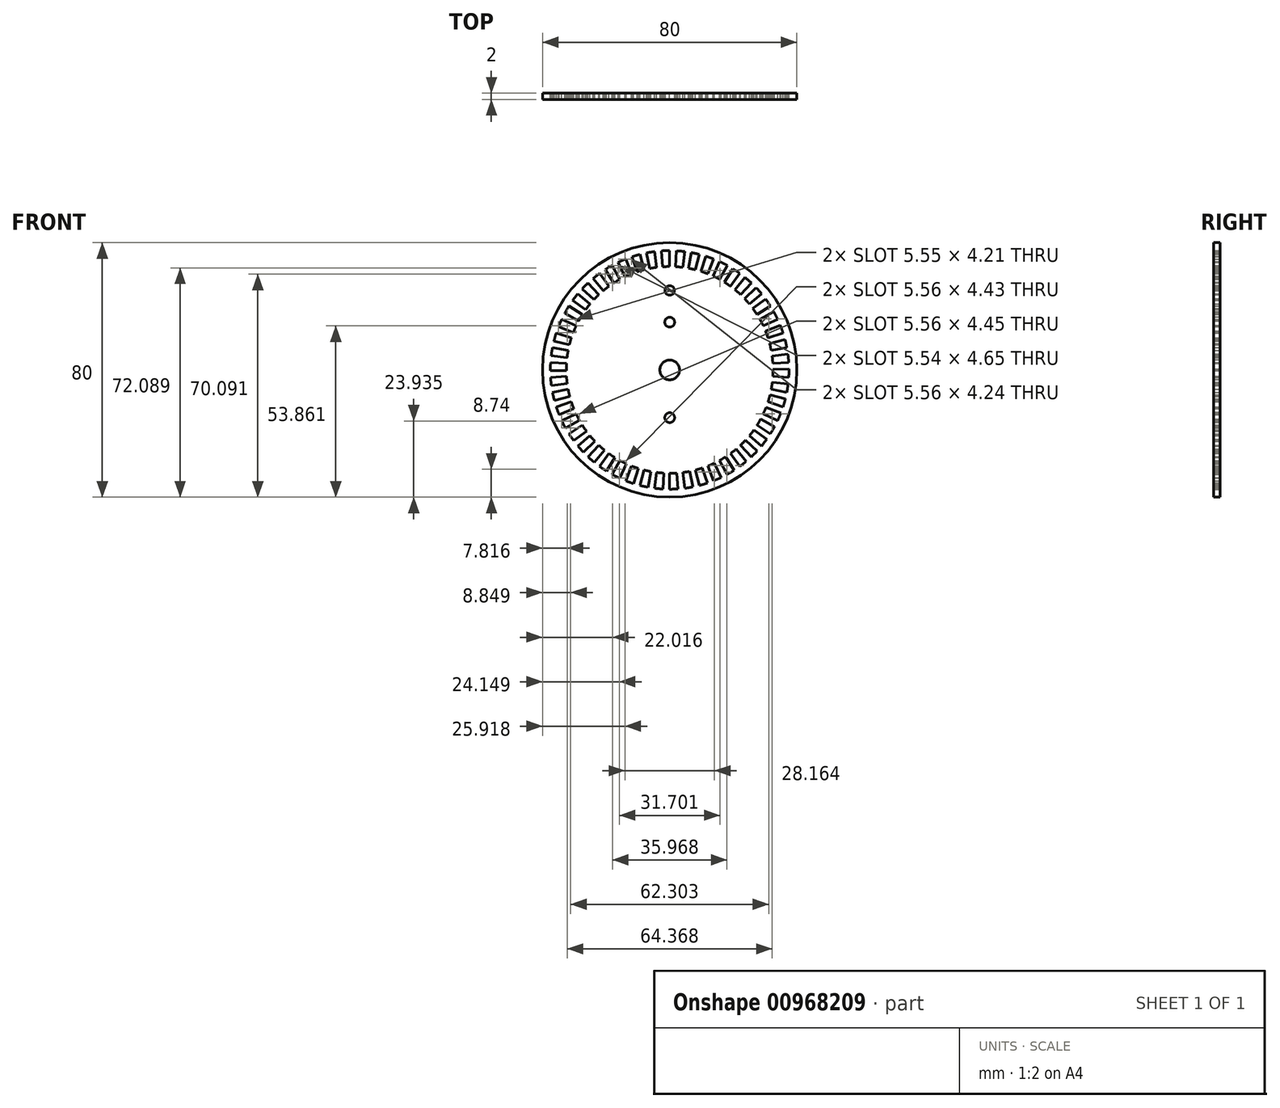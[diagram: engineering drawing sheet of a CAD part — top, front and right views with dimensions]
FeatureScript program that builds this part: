
annotation { "Feature Type Name" : "Feature", "Feature Type Description" : "" }
export const myFeature = defineFeature(function(context is Context, id is Id, definition is map)
    precondition{}
    {
        {
            var Q0;
            Q0=qCreatedBy(makeId("Front.planeOp"),FACE);
            var sketch = newSketch(context, id + "F0", { "sketchPlane" : qUnion([Q0])});
            skCircle(sketch, "E0", {"center": v(0, 0) * mm, "radius": 40 * mm});
            skSolve(sketch);
        }
        {
            var Q0;
            Q0 = qSketchRegion(id + "F0", true);
            extrude(context, id + "F1", {"entities" : qUnion([Q0]), "endBound" : BoundingType.SYMMETRIC, "depth" : 2 * mm, "offsetDistance" : 25 * mm});
        }
        {
            var Q0;
            Q0=qCreatedBy(makeId("Front.planeOp"),FACE);
            var sketch = newSketch(context, id + "F2", { "sketchPlane" : qUnion([Q0])});
            skCircle(sketch, "E1", {"center": v(0, 0) * mm, "radius": 3.1 * mm});
            skCircle(sketch, "E2", {"center": v(0, 25) * mm, "radius": 1.5 * mm});
            skCircle(sketch, "E3", {"center": v(0, 15) * mm, "radius": 1.55 * mm});
            skCircle(sketch, "E4", {"center": v(0, -15) * mm, "radius": 1.55 * mm});
            skSolve(sketch);
        }
        {
            var Q0;
            Q0 = qSketchRegion(id + "F2", true);
            extrude(context, id + "F3", {"entities" : qUnion([Q0]), "operationType" : NewBodyOperationType.REMOVE, "endBound" : BoundingType.SYMMETRIC, "oppositeDirection" : true, "depth" : 12 * mm, "offsetDistance" : 25 * mm});
        }
        {
            var Q0;
            Q0=qCreatedBy(makeId("Front.planeOp"),FACE);
            var sketch = newSketch(context, id + "F4", { "sketchPlane" : qUnion([Q0])});
            skLineSegment(sketch, "E5", {"start": v(0, 32.5) * mm, "end": v(0, 37.5) * mm});
            skArc(sketch, "E6", {"start": v(0, 37.5) * mm, "mid": v(-1.3, 37.48) * mm, "end": v(-2.61, 37.4) * mm});
            skArc(sketch, "E7", {"start": v(0, 32.5) * mm, "mid": v(-1.13, 32.48) * mm, "end": v(-2.26, 32.42) * mm});
            skLineSegment(sketch, "E8", {"start": v(-2.26, 32.42) * mm, "end": v(-2.61, 37.4) * mm});
            skLineSegment(sketch, "E9.1.0", {"start": v(-6.3, 31.88) * mm, "end": v(-7.28, 36.79) * mm});
            skLineSegment(sketch, "E9.1.1", {"start": v(-4.07, 32.24) * mm, "end": v(-4.7, 37.2) * mm});
            skArc(sketch, "E9.1.2", {"start": v(-4.7, 37.2) * mm, "mid": v(-6, 37.02) * mm, "end": v(-7.28, 36.79) * mm});
            skArc(sketch, "E9.1.3", {"start": v(-4.07, 32.24) * mm, "mid": v(-5.2, 32.08) * mm, "end": v(-6.3, 31.88) * mm});
            skLineSegment(sketch, "E9.2.0", {"start": v(-10.26, 30.84) * mm, "end": v(-11.83, 35.58) * mm});
            skLineSegment(sketch, "E9.2.1", {"start": v(-8.08, 31.48) * mm, "end": v(-9.33, 36.32) * mm});
            skArc(sketch, "E9.2.2", {"start": v(-9.33, 36.32) * mm, "mid": v(-10.59, 35.97) * mm, "end": v(-11.83, 35.58) * mm});
            skArc(sketch, "E9.2.3", {"start": v(-8.08, 31.48) * mm, "mid": v(-9.17, 31.18) * mm, "end": v(-10.26, 30.84) * mm});
            skLineSegment(sketch, "E9.3.0", {"start": v(-14.04, 29.31) * mm, "end": v(-16.2, 33.82) * mm});
            skLineSegment(sketch, "E9.3.1", {"start": v(-11.96, 30.22) * mm, "end": v(-13.8, 34.87) * mm});
            skArc(sketch, "E9.3.2", {"start": v(-13.8, 34.87) * mm, "mid": v(-15.01, 34.36) * mm, "end": v(-16.2, 33.82) * mm});
            skArc(sketch, "E9.3.3", {"start": v(-11.96, 30.22) * mm, "mid": v(-13, 29.78) * mm, "end": v(-14.04, 29.31) * mm});
            skLineSegment(sketch, "E9.4.0", {"start": v(-17.6, 27.32) * mm, "end": v(-20.31, 31.52) * mm});
            skLineSegment(sketch, "E9.4.1", {"start": v(-15.66, 28.48) * mm, "end": v(-18.07, 32.86) * mm});
            skArc(sketch, "E9.4.2", {"start": v(-18.07, 32.86) * mm, "mid": v(-19.2, 32.21) * mm, "end": v(-20.31, 31.52) * mm});
            skArc(sketch, "E9.4.3", {"start": v(-15.66, 28.48) * mm, "mid": v(-16.64, 27.92) * mm, "end": v(-17.6, 27.32) * mm});
            skLineSegment(sketch, "E9.5.0", {"start": v(-20.89, 24.9) * mm, "end": v(-24.1, 28.73) * mm});
            skLineSegment(sketch, "E9.5.1", {"start": v(-19.1, 26.3) * mm, "end": v(-22.04, 30.34) * mm});
            skArc(sketch, "E9.5.2", {"start": v(-22.04, 30.34) * mm, "mid": v(-23.09, 29.55) * mm, "end": v(-24.1, 28.73) * mm});
            skArc(sketch, "E9.5.3", {"start": v(-19.1, 26.3) * mm, "mid": v(-20, 25.61) * mm, "end": v(-20.89, 24.9) * mm});
            skLineSegment(sketch, "E9.6.0", {"start": v(-23.84, 22.08) * mm, "end": v(-27.51, 25.48) * mm});
            skLineSegment(sketch, "E9.6.1", {"start": v(-22.25, 23.7) * mm, "end": v(-25.67, 27.34) * mm});
            skArc(sketch, "E9.6.2", {"start": v(-25.67, 27.34) * mm, "mid": v(-26.6, 26.43) * mm, "end": v(-27.51, 25.48) * mm});
            skArc(sketch, "E9.6.3", {"start": v(-22.25, 23.7) * mm, "mid": v(-23.06, 22.9) * mm, "end": v(-23.84, 22.08) * mm});
            skLineSegment(sketch, "E9.7.0", {"start": v(-26.42, 18.92) * mm, "end": v(-30.49, 21.83) * mm});
            skLineSegment(sketch, "E9.7.1", {"start": v(-25.04, 20.72) * mm, "end": v(-28.9, 23.9) * mm});
            skArc(sketch, "E9.7.2", {"start": v(-28.9, 23.9) * mm, "mid": v(-29.7, 22.88) * mm, "end": v(-30.49, 21.83) * mm});
            skArc(sketch, "E9.7.3", {"start": v(-25.04, 20.72) * mm, "mid": v(-25.75, 19.83) * mm, "end": v(-26.42, 18.92) * mm});
            skLineSegment(sketch, "E9.8.0", {"start": v(-28.59, 15.46) * mm, "end": v(-32.98, 17.84) * mm});
            skLineSegment(sketch, "E9.8.1", {"start": v(-27.44, 17.41) * mm, "end": v(-31.66, 20.1) * mm});
            skArc(sketch, "E9.8.2", {"start": v(-31.66, 20.1) * mm, "mid": v(-32.34, 18.98) * mm, "end": v(-32.98, 17.84) * mm});
            skArc(sketch, "E9.8.3", {"start": v(-27.44, 17.41) * mm, "mid": v(-28.03, 16.45) * mm, "end": v(-28.59, 15.46) * mm});
            skLineSegment(sketch, "E9.9.0", {"start": v(-30.3, 11.76) * mm, "end": v(-34.96, 13.56) * mm});
            skLineSegment(sketch, "E9.9.1", {"start": v(-29.4, 13.84) * mm, "end": v(-33.93, 15.97) * mm});
            skArc(sketch, "E9.9.2", {"start": v(-33.93, 15.97) * mm, "mid": v(-34.47, 14.77) * mm, "end": v(-34.96, 13.56) * mm});
            skArc(sketch, "E9.9.3", {"start": v(-29.4, 13.84) * mm, "mid": v(-29.87, 12.8) * mm, "end": v(-30.3, 11.76) * mm});
            skLineSegment(sketch, "E9.10.0", {"start": v(-31.53, 7.87) * mm, "end": v(-36.39, 9.08) * mm});
            skLineSegment(sketch, "E9.10.1", {"start": v(-30.9, 10.04) * mm, "end": v(-35.66, 11.59) * mm});
            skArc(sketch, "E9.10.2", {"start": v(-35.66, 11.59) * mm, "mid": v(-36.05, 10.34) * mm, "end": v(-36.39, 9.08) * mm});
            skArc(sketch, "E9.10.3", {"start": v(-30.9, 10.04) * mm, "mid": v(-31.24, 8.96) * mm, "end": v(-31.53, 7.87) * mm});
            skLineSegment(sketch, "E9.11.0", {"start": v(-32.27, 3.85) * mm, "end": v(-37.24, 4.44) * mm});
            skLineSegment(sketch, "E9.11.1", {"start": v(-31.92, 6.09) * mm, "end": v(-36.84, 7.03) * mm});
            skArc(sketch, "E9.11.2", {"start": v(-36.84, 7.03) * mm, "mid": v(-37.06, 5.74) * mm, "end": v(-37.24, 4.44) * mm});
            skArc(sketch, "E9.11.3", {"start": v(-31.92, 6.09) * mm, "mid": v(-32.12, 4.97) * mm, "end": v(-32.27, 3.85) * mm});
            skLineSegment(sketch, "E9.12.0", {"start": v(-32.5, -0.22) * mm, "end": v(-37.5, -0.26) * mm});
            skLineSegment(sketch, "E9.12.1", {"start": v(-32.44, 2.04) * mm, "end": v(-37.43, 2.35) * mm});
            skArc(sketch, "E9.12.2", {"start": v(-37.43, 2.35) * mm, "mid": v(-37.49, 1.05) * mm, "end": v(-37.5, -0.26) * mm});
            skArc(sketch, "E9.12.3", {"start": v(-32.44, 2.04) * mm, "mid": v(-32.49, 0.9) * mm, "end": v(-32.5, -0.22) * mm});
            skLineSegment(sketch, "E9.13.0", {"start": v(-32.21, -4.3) * mm, "end": v(-37.17, -4.96) * mm});
            skLineSegment(sketch, "E9.13.1", {"start": v(-32.44, -2.04) * mm, "end": v(-37.43, -2.35) * mm});
            skArc(sketch, "E9.13.2", {"start": v(-37.43, -2.35) * mm, "mid": v(-37.32, -3.66) * mm, "end": v(-37.17, -4.96) * mm});
            skArc(sketch, "E9.13.3", {"start": v(-32.44, -2.04) * mm, "mid": v(-32.35, -3.17) * mm, "end": v(-32.21, -4.3) * mm});
            skLineSegment(sketch, "E9.14.0", {"start": v(-31.42, -8.3) * mm, "end": v(-36.26, -9.58) * mm});
            skLineSegment(sketch, "E9.14.1", {"start": v(-31.92, -6.09) * mm, "end": v(-36.84, -7.03) * mm});
            skArc(sketch, "E9.14.2", {"start": v(-36.84, -7.03) * mm, "mid": v(-36.57, -8.3) * mm, "end": v(-36.26, -9.58) * mm});
            skArc(sketch, "E9.14.3", {"start": v(-31.92, -6.09) * mm, "mid": v(-31.7, -7.2) * mm, "end": v(-31.42, -8.3) * mm});
            skLineSegment(sketch, "E9.15.0", {"start": v(-30.13, -12.17) * mm, "end": v(-34.77, -14.04) * mm});
            skLineSegment(sketch, "E9.15.1", {"start": v(-30.9, -10.04) * mm, "end": v(-35.66, -11.59) * mm});
            skArc(sketch, "E9.15.2", {"start": v(-35.66, -11.59) * mm, "mid": v(-35.24, -12.82) * mm, "end": v(-34.77, -14.04) * mm});
            skArc(sketch, "E9.15.3", {"start": v(-30.9, -10.04) * mm, "mid": v(-30.54, -11.11) * mm, "end": v(-30.13, -12.17) * mm});
            skLineSegment(sketch, "E9.16.0", {"start": v(-28.37, -15.85) * mm, "end": v(-32.74, -18.3) * mm});
            skLineSegment(sketch, "E9.16.1", {"start": v(-29.4, -13.84) * mm, "end": v(-33.93, -15.97) * mm});
            skArc(sketch, "E9.16.2", {"start": v(-33.93, -15.97) * mm, "mid": v(-33.35, -17.14) * mm, "end": v(-32.74, -18.3) * mm});
            skArc(sketch, "E9.16.3", {"start": v(-29.4, -13.84) * mm, "mid": v(-28.9, -14.85) * mm, "end": v(-28.37, -15.85) * mm});
            skLineSegment(sketch, "E9.17.0", {"start": v(-26.16, -19.28) * mm, "end": v(-30.19, -22.25) * mm});
            skLineSegment(sketch, "E9.17.1", {"start": v(-27.44, -17.41) * mm, "end": v(-31.66, -20.1) * mm});
            skArc(sketch, "E9.17.2", {"start": v(-31.66, -20.1) * mm, "mid": v(-30.94, -21.18) * mm, "end": v(-30.19, -22.25) * mm});
            skArc(sketch, "E9.17.3", {"start": v(-27.44, -17.41) * mm, "mid": v(-26.82, -18.36) * mm, "end": v(-26.16, -19.28) * mm});
            skLineSegment(sketch, "E9.18.0", {"start": v(-23.54, -22.41) * mm, "end": v(-27.16, -25.86) * mm});
            skLineSegment(sketch, "E9.18.1", {"start": v(-25.04, -20.72) * mm, "end": v(-28.9, -23.9) * mm});
            skArc(sketch, "E9.18.2", {"start": v(-28.9, -23.9) * mm, "mid": v(-28.04, -24.9) * mm, "end": v(-27.16, -25.86) * mm});
            skArc(sketch, "E9.18.3", {"start": v(-25.04, -20.72) * mm, "mid": v(-24.3, -21.58) * mm, "end": v(-23.54, -22.41) * mm});
            skLineSegment(sketch, "E9.19.0", {"start": v(-20.54, -25.18) * mm, "end": v(-23.7, -29.06) * mm});
            skLineSegment(sketch, "E9.19.1", {"start": v(-22.25, -23.7) * mm, "end": v(-25.67, -27.34) * mm});
            skArc(sketch, "E9.19.2", {"start": v(-25.67, -27.34) * mm, "mid": v(-24.7, -28.21) * mm, "end": v(-23.7, -29.06) * mm});
            skArc(sketch, "E9.19.3", {"start": v(-22.25, -23.7) * mm, "mid": v(-21.4, -24.45) * mm, "end": v(-20.54, -25.18) * mm});
            skLineSegment(sketch, "E9.20.0", {"start": v(-17.23, -27.56) * mm, "end": v(-19.88, -31.8) * mm});
            skLineSegment(sketch, "E9.20.1", {"start": v(-19.1, -26.3) * mm, "end": v(-22.04, -30.34) * mm});
            skArc(sketch, "E9.20.2", {"start": v(-22.04, -30.34) * mm, "mid": v(-20.97, -31.09) * mm, "end": v(-19.88, -31.8) * mm});
            skArc(sketch, "E9.20.3", {"start": v(-19.1, -26.3) * mm, "mid": v(-18.18, -26.94) * mm, "end": v(-17.23, -27.56) * mm});
            skLineSegment(sketch, "E9.21.0", {"start": v(-13.64, -29.5) * mm, "end": v(-15.73, -34.04) * mm});
            skLineSegment(sketch, "E9.21.1", {"start": v(-15.66, -28.48) * mm, "end": v(-18.07, -32.86) * mm});
            skArc(sketch, "E9.21.2", {"start": v(-18.07, -32.86) * mm, "mid": v(-16.9, -33.47) * mm, "end": v(-15.73, -34.04) * mm});
            skArc(sketch, "E9.21.3", {"start": v(-15.66, -28.48) * mm, "mid": v(-14.66, -29) * mm, "end": v(-13.64, -29.5) * mm});
            skLineSegment(sketch, "E9.22.0", {"start": v(-9.83, -30.98) * mm, "end": v(-11.34, -35.74) * mm});
            skLineSegment(sketch, "E9.22.1", {"start": v(-11.96, -30.22) * mm, "end": v(-13.8, -34.87) * mm});
            skArc(sketch, "E9.22.2", {"start": v(-13.8, -34.87) * mm, "mid": v(-12.58, -35.33) * mm, "end": v(-11.34, -35.74) * mm});
            skArc(sketch, "E9.22.3", {"start": v(-11.96, -30.22) * mm, "mid": v(-10.9, -30.62) * mm, "end": v(-9.83, -30.98) * mm});
            skLineSegment(sketch, "E9.23.0", {"start": v(-5.87, -31.97) * mm, "end": v(-6.77, -36.88) * mm});
            skLineSegment(sketch, "E9.23.1", {"start": v(-8.08, -31.48) * mm, "end": v(-9.33, -36.32) * mm});
            skArc(sketch, "E9.23.2", {"start": v(-9.33, -36.32) * mm, "mid": v(-8.05, -36.62) * mm, "end": v(-6.77, -36.88) * mm});
            skArc(sketch, "E9.23.3", {"start": v(-8.08, -31.48) * mm, "mid": v(-6.98, -31.74) * mm, "end": v(-5.87, -31.97) * mm});
            skLineSegment(sketch, "E9.24.0", {"start": v(-1.82, -32.45) * mm, "end": v(-2.1, -37.44) * mm});
            skLineSegment(sketch, "E9.24.1", {"start": v(-4.07, -32.24) * mm, "end": v(-4.7, -37.2) * mm});
            skArc(sketch, "E9.24.2", {"start": v(-4.7, -37.2) * mm, "mid": v(-3.4, -37.35) * mm, "end": v(-2.1, -37.44) * mm});
            skArc(sketch, "E9.24.3", {"start": v(-4.07, -32.24) * mm, "mid": v(-2.95, -32.37) * mm, "end": v(-1.82, -32.45) * mm});
            skLineSegment(sketch, "E9.25.0", {"start": v(2.26, -32.42) * mm, "end": v(2.61, -37.4) * mm});
            skLineSegment(sketch, "E9.25.1", {"start": v(0, -32.5) * mm, "end": v(0, -37.5) * mm});
            skArc(sketch, "E9.25.2", {"start": v(0, -37.5) * mm, "mid": v(1.3, -37.48) * mm, "end": v(2.61, -37.4) * mm});
            skArc(sketch, "E9.25.3", {"start": v(0, -32.5) * mm, "mid": v(1.13, -32.48) * mm, "end": v(2.26, -32.42) * mm});
            skLineSegment(sketch, "E9.26.0", {"start": v(6.3, -31.88) * mm, "end": v(7.28, -36.79) * mm});
            skLineSegment(sketch, "E9.26.1", {"start": v(4.07, -32.24) * mm, "end": v(4.7, -37.2) * mm});
            skArc(sketch, "E9.26.2", {"start": v(4.7, -37.2) * mm, "mid": v(6, -37.02) * mm, "end": v(7.28, -36.79) * mm});
            skArc(sketch, "E9.26.3", {"start": v(4.07, -32.24) * mm, "mid": v(5.2, -32.08) * mm, "end": v(6.3, -31.88) * mm});
            skLineSegment(sketch, "E9.27.0", {"start": v(10.26, -30.84) * mm, "end": v(11.83, -35.58) * mm});
            skLineSegment(sketch, "E9.27.1", {"start": v(8.08, -31.48) * mm, "end": v(9.33, -36.32) * mm});
            skArc(sketch, "E9.27.2", {"start": v(9.33, -36.32) * mm, "mid": v(10.59, -35.97) * mm, "end": v(11.83, -35.58) * mm});
            skArc(sketch, "E9.27.3", {"start": v(8.08, -31.48) * mm, "mid": v(9.17, -31.18) * mm, "end": v(10.26, -30.84) * mm});
            skLineSegment(sketch, "E9.28.0", {"start": v(14.04, -29.31) * mm, "end": v(16.2, -33.82) * mm});
            skLineSegment(sketch, "E9.28.1", {"start": v(11.96, -30.22) * mm, "end": v(13.8, -34.87) * mm});
            skArc(sketch, "E9.28.2", {"start": v(13.8, -34.87) * mm, "mid": v(15.01, -34.36) * mm, "end": v(16.2, -33.82) * mm});
            skArc(sketch, "E9.28.3", {"start": v(11.96, -30.22) * mm, "mid": v(13, -29.78) * mm, "end": v(14.04, -29.31) * mm});
            skLineSegment(sketch, "E9.29.0", {"start": v(17.6, -27.32) * mm, "end": v(20.31, -31.52) * mm});
            skLineSegment(sketch, "E9.29.1", {"start": v(15.66, -28.48) * mm, "end": v(18.07, -32.86) * mm});
            skArc(sketch, "E9.29.2", {"start": v(18.07, -32.86) * mm, "mid": v(19.2, -32.21) * mm, "end": v(20.31, -31.52) * mm});
            skArc(sketch, "E9.29.3", {"start": v(15.66, -28.48) * mm, "mid": v(16.64, -27.92) * mm, "end": v(17.6, -27.32) * mm});
            skLineSegment(sketch, "E9.30.0", {"start": v(20.89, -24.9) * mm, "end": v(24.1, -28.73) * mm});
            skLineSegment(sketch, "E9.30.1", {"start": v(19.1, -26.3) * mm, "end": v(22.04, -30.34) * mm});
            skArc(sketch, "E9.30.2", {"start": v(22.04, -30.34) * mm, "mid": v(23.09, -29.55) * mm, "end": v(24.1, -28.73) * mm});
            skArc(sketch, "E9.30.3", {"start": v(19.1, -26.3) * mm, "mid": v(20, -25.61) * mm, "end": v(20.89, -24.9) * mm});
            skLineSegment(sketch, "E9.31.0", {"start": v(23.84, -22.08) * mm, "end": v(27.51, -25.48) * mm});
            skLineSegment(sketch, "E9.31.1", {"start": v(22.25, -23.7) * mm, "end": v(25.67, -27.34) * mm});
            skArc(sketch, "E9.31.2", {"start": v(25.67, -27.34) * mm, "mid": v(26.6, -26.43) * mm, "end": v(27.51, -25.48) * mm});
            skArc(sketch, "E9.31.3", {"start": v(22.25, -23.7) * mm, "mid": v(23.06, -22.9) * mm, "end": v(23.84, -22.08) * mm});
            skLineSegment(sketch, "E9.32.0", {"start": v(26.42, -18.92) * mm, "end": v(30.49, -21.83) * mm});
            skLineSegment(sketch, "E9.32.1", {"start": v(25.04, -20.72) * mm, "end": v(28.9, -23.9) * mm});
            skArc(sketch, "E9.32.2", {"start": v(28.9, -23.9) * mm, "mid": v(29.7, -22.88) * mm, "end": v(30.49, -21.83) * mm});
            skArc(sketch, "E9.32.3", {"start": v(25.04, -20.72) * mm, "mid": v(25.75, -19.83) * mm, "end": v(26.42, -18.92) * mm});
            skLineSegment(sketch, "E9.33.0", {"start": v(28.59, -15.46) * mm, "end": v(32.98, -17.84) * mm});
            skLineSegment(sketch, "E9.33.1", {"start": v(27.44, -17.41) * mm, "end": v(31.66, -20.1) * mm});
            skArc(sketch, "E9.33.2", {"start": v(31.66, -20.1) * mm, "mid": v(32.34, -18.98) * mm, "end": v(32.98, -17.84) * mm});
            skArc(sketch, "E9.33.3", {"start": v(27.44, -17.41) * mm, "mid": v(28.03, -16.45) * mm, "end": v(28.59, -15.46) * mm});
            skLineSegment(sketch, "E9.34.0", {"start": v(30.3, -11.76) * mm, "end": v(34.96, -13.56) * mm});
            skLineSegment(sketch, "E9.34.1", {"start": v(29.4, -13.84) * mm, "end": v(33.93, -15.97) * mm});
            skArc(sketch, "E9.34.2", {"start": v(33.93, -15.97) * mm, "mid": v(34.47, -14.77) * mm, "end": v(34.96, -13.56) * mm});
            skArc(sketch, "E9.34.3", {"start": v(29.4, -13.84) * mm, "mid": v(29.87, -12.8) * mm, "end": v(30.3, -11.76) * mm});
            skLineSegment(sketch, "E9.35.0", {"start": v(31.53, -7.87) * mm, "end": v(36.39, -9.08) * mm});
            skLineSegment(sketch, "E9.35.1", {"start": v(30.9, -10.04) * mm, "end": v(35.66, -11.59) * mm});
            skArc(sketch, "E9.35.2", {"start": v(35.66, -11.59) * mm, "mid": v(36.05, -10.34) * mm, "end": v(36.39, -9.08) * mm});
            skArc(sketch, "E9.35.3", {"start": v(30.9, -10.04) * mm, "mid": v(31.24, -8.96) * mm, "end": v(31.53, -7.87) * mm});
            skLineSegment(sketch, "E9.36.0", {"start": v(32.27, -3.85) * mm, "end": v(37.24, -4.44) * mm});
            skLineSegment(sketch, "E9.36.1", {"start": v(31.92, -6.09) * mm, "end": v(36.84, -7.03) * mm});
            skArc(sketch, "E9.36.2", {"start": v(36.84, -7.03) * mm, "mid": v(37.06, -5.74) * mm, "end": v(37.24, -4.44) * mm});
            skArc(sketch, "E9.36.3", {"start": v(31.92, -6.09) * mm, "mid": v(32.12, -4.97) * mm, "end": v(32.27, -3.85) * mm});
            skLineSegment(sketch, "E9.37.0", {"start": v(32.5, 0.22) * mm, "end": v(37.5, 0.26) * mm});
            skLineSegment(sketch, "E9.37.1", {"start": v(32.44, -2.04) * mm, "end": v(37.43, -2.35) * mm});
            skArc(sketch, "E9.37.2", {"start": v(37.43, -2.35) * mm, "mid": v(37.49, -1.05) * mm, "end": v(37.5, 0.26) * mm});
            skArc(sketch, "E9.37.3", {"start": v(32.44, -2.04) * mm, "mid": v(32.49, -0.9) * mm, "end": v(32.5, 0.22) * mm});
            skLineSegment(sketch, "E9.38.0", {"start": v(32.21, 4.3) * mm, "end": v(37.17, 4.96) * mm});
            skLineSegment(sketch, "E9.38.1", {"start": v(32.44, 2.04) * mm, "end": v(37.43, 2.35) * mm});
            skArc(sketch, "E9.38.2", {"start": v(37.43, 2.35) * mm, "mid": v(37.32, 3.66) * mm, "end": v(37.17, 4.96) * mm});
            skArc(sketch, "E9.38.3", {"start": v(32.44, 2.04) * mm, "mid": v(32.35, 3.17) * mm, "end": v(32.21, 4.3) * mm});
            skLineSegment(sketch, "E9.39.0", {"start": v(31.42, 8.3) * mm, "end": v(36.26, 9.58) * mm});
            skLineSegment(sketch, "E9.39.1", {"start": v(31.92, 6.09) * mm, "end": v(36.84, 7.03) * mm});
            skArc(sketch, "E9.39.2", {"start": v(36.84, 7.03) * mm, "mid": v(36.57, 8.3) * mm, "end": v(36.26, 9.58) * mm});
            skArc(sketch, "E9.39.3", {"start": v(31.92, 6.09) * mm, "mid": v(31.7, 7.2) * mm, "end": v(31.42, 8.3) * mm});
            skLineSegment(sketch, "E9.40.0", {"start": v(30.13, 12.17) * mm, "end": v(34.77, 14.04) * mm});
            skLineSegment(sketch, "E9.40.1", {"start": v(30.9, 10.04) * mm, "end": v(35.66, 11.59) * mm});
            skArc(sketch, "E9.40.2", {"start": v(35.66, 11.59) * mm, "mid": v(35.24, 12.82) * mm, "end": v(34.77, 14.04) * mm});
            skArc(sketch, "E9.40.3", {"start": v(30.9, 10.04) * mm, "mid": v(30.54, 11.11) * mm, "end": v(30.13, 12.17) * mm});
            skLineSegment(sketch, "E9.41.0", {"start": v(28.37, 15.85) * mm, "end": v(32.74, 18.3) * mm});
            skLineSegment(sketch, "E9.41.1", {"start": v(29.4, 13.84) * mm, "end": v(33.93, 15.97) * mm});
            skArc(sketch, "E9.41.2", {"start": v(33.93, 15.97) * mm, "mid": v(33.35, 17.14) * mm, "end": v(32.74, 18.3) * mm});
            skArc(sketch, "E9.41.3", {"start": v(29.4, 13.84) * mm, "mid": v(28.9, 14.85) * mm, "end": v(28.37, 15.85) * mm});
            skLineSegment(sketch, "E9.42.0", {"start": v(26.16, 19.28) * mm, "end": v(30.19, 22.25) * mm});
            skLineSegment(sketch, "E9.42.1", {"start": v(27.44, 17.41) * mm, "end": v(31.66, 20.1) * mm});
            skArc(sketch, "E9.42.2", {"start": v(31.66, 20.1) * mm, "mid": v(30.94, 21.18) * mm, "end": v(30.19, 22.25) * mm});
            skArc(sketch, "E9.42.3", {"start": v(27.44, 17.41) * mm, "mid": v(26.82, 18.36) * mm, "end": v(26.16, 19.28) * mm});
            skLineSegment(sketch, "E9.43.0", {"start": v(23.54, 22.41) * mm, "end": v(27.16, 25.86) * mm});
            skLineSegment(sketch, "E9.43.1", {"start": v(25.04, 20.72) * mm, "end": v(28.9, 23.9) * mm});
            skArc(sketch, "E9.43.2", {"start": v(28.9, 23.9) * mm, "mid": v(28.04, 24.9) * mm, "end": v(27.16, 25.86) * mm});
            skArc(sketch, "E9.43.3", {"start": v(25.04, 20.72) * mm, "mid": v(24.3, 21.58) * mm, "end": v(23.54, 22.41) * mm});
            skLineSegment(sketch, "E9.44.0", {"start": v(20.54, 25.18) * mm, "end": v(23.7, 29.06) * mm});
            skLineSegment(sketch, "E9.44.1", {"start": v(22.25, 23.7) * mm, "end": v(25.67, 27.34) * mm});
            skArc(sketch, "E9.44.2", {"start": v(25.67, 27.34) * mm, "mid": v(24.7, 28.21) * mm, "end": v(23.7, 29.06) * mm});
            skArc(sketch, "E9.44.3", {"start": v(22.25, 23.7) * mm, "mid": v(21.4, 24.45) * mm, "end": v(20.54, 25.18) * mm});
            skLineSegment(sketch, "E9.45.0", {"start": v(17.23, 27.56) * mm, "end": v(19.88, 31.8) * mm});
            skLineSegment(sketch, "E9.45.1", {"start": v(19.1, 26.3) * mm, "end": v(22.04, 30.34) * mm});
            skArc(sketch, "E9.45.2", {"start": v(22.04, 30.34) * mm, "mid": v(20.97, 31.09) * mm, "end": v(19.88, 31.8) * mm});
            skArc(sketch, "E9.45.3", {"start": v(19.1, 26.3) * mm, "mid": v(18.18, 26.94) * mm, "end": v(17.23, 27.56) * mm});
            skLineSegment(sketch, "E9.46.0", {"start": v(13.64, 29.5) * mm, "end": v(15.73, 34.04) * mm});
            skLineSegment(sketch, "E9.46.1", {"start": v(15.66, 28.48) * mm, "end": v(18.07, 32.86) * mm});
            skArc(sketch, "E9.46.2", {"start": v(18.07, 32.86) * mm, "mid": v(16.9, 33.47) * mm, "end": v(15.73, 34.04) * mm});
            skArc(sketch, "E9.46.3", {"start": v(15.66, 28.48) * mm, "mid": v(14.66, 29) * mm, "end": v(13.64, 29.5) * mm});
            skLineSegment(sketch, "E9.47.0", {"start": v(9.83, 30.98) * mm, "end": v(11.34, 35.74) * mm});
            skLineSegment(sketch, "E9.47.1", {"start": v(11.96, 30.22) * mm, "end": v(13.8, 34.87) * mm});
            skArc(sketch, "E9.47.2", {"start": v(13.8, 34.87) * mm, "mid": v(12.58, 35.33) * mm, "end": v(11.34, 35.74) * mm});
            skArc(sketch, "E9.47.3", {"start": v(11.96, 30.22) * mm, "mid": v(10.9, 30.62) * mm, "end": v(9.83, 30.98) * mm});
            skLineSegment(sketch, "E9.48.0", {"start": v(5.87, 31.97) * mm, "end": v(6.77, 36.88) * mm});
            skLineSegment(sketch, "E9.48.1", {"start": v(8.08, 31.48) * mm, "end": v(9.33, 36.32) * mm});
            skArc(sketch, "E9.48.2", {"start": v(9.33, 36.32) * mm, "mid": v(8.05, 36.62) * mm, "end": v(6.77, 36.88) * mm});
            skArc(sketch, "E9.48.3", {"start": v(8.08, 31.48) * mm, "mid": v(6.98, 31.74) * mm, "end": v(5.87, 31.97) * mm});
            skLineSegment(sketch, "E9.49.0", {"start": v(1.82, 32.45) * mm, "end": v(2.1, 37.44) * mm});
            skLineSegment(sketch, "E9.49.1", {"start": v(4.07, 32.24) * mm, "end": v(4.7, 37.2) * mm});
            skArc(sketch, "E9.49.2", {"start": v(4.7, 37.2) * mm, "mid": v(3.4, 37.35) * mm, "end": v(2.1, 37.44) * mm});
            skArc(sketch, "E9.49.3", {"start": v(4.07, 32.24) * mm, "mid": v(2.95, 32.37) * mm, "end": v(1.82, 32.45) * mm});
            skSolve(sketch);
        }
        {
            var Q0;
            Q0 = qSketchRegion(id + "F4", true);
            extrude(context, id + "F5", {"entities" : qUnion([Q0]), "operationType" : NewBodyOperationType.REMOVE, "endBound" : BoundingType.SYMMETRIC, "depth" : 25 * mm, "offsetDistance" : 25 * mm});
        }
    });
